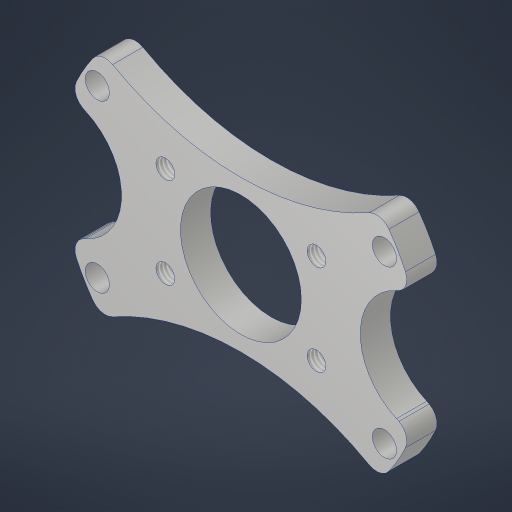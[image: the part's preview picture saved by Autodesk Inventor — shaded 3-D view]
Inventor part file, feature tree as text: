
AUTODESK INVENTOR PART (.ipt)
format: ipt  version: 2023.4 (Build 274418000, 418)  size: 342,528 bytes
history: native  units: in
note: dims shown in document units (in); Inventor stores cm internally (conversion verified against a paired STEP export)
features: sketch x5, extrude x4, hole x2, fillet x1, thicken_offset x1, projected_geometry x1
ambient origin geometry x8: Origin, YZ Plane, XZ Plane, XY Plane, X Axis, Y Axis, Z Axis, Center Point
bodies: Solid1 (feature_tree)
feature tree (14):
  sketch  "Sketch1"  dims[d0=2.375in d1=1.375in d2=0.5in]
  extrude  "Extrusion1"  Depth=1.375in
  fillet  "Fillet1"  Radius=0.5in
  hole  "Hole1"  [1 undecoded]
  extrude  "Extrusion2"  Depth=0.5in
  hole  "Hole2"  [1 undecoded]
  extrude  "Extrusion3"  Depth=0.125in
  extrude  "Extrusion4"  Depth=0.25in TaperAngle=0.0deg
  thicken_offset  "Thicken1"
  sketch  "Sketch3"  dims[d3=0.5in d4=0.5in]
  sketch  "Sketch4"  dims[d5=0.5in d6=1.25in]
  sketch  "Sketch5"  dims[d7=0.5in d8=0.5in]
  sketch  "Sketch6"  dims[d9=0.125in d10=0.125in d11=0.75in d12=0.0in d13=0.125in d14=0.201in d15=0.75in d16=0.385in d17=0.25in d18=0.5635in d19=1.0in d20=0.8108in d21=1.885in d22=0.125in d23=0.0in d24=0.125in d25=0.125in d26=0.125in d27=3.0in d28=1.0in d29=1.25in d30=0.75in d31=0.156in d32=0.38in d33=0.119in d34=0.25in d35=0.5635in d36=1.0in d37=0.8108in d38=2.25in d39=0.6875in d40=0.0in d41=0.8999in d42=0.0in d43=0.1875in d44=0.0625in]
  projected_geometry  "Project Cut Edges1"
note: 2 required parameter values undecoded (feature->parameter linkage not recoverable at this tier; creation-order binding heuristic only, values carry confidence <= 0.55)
